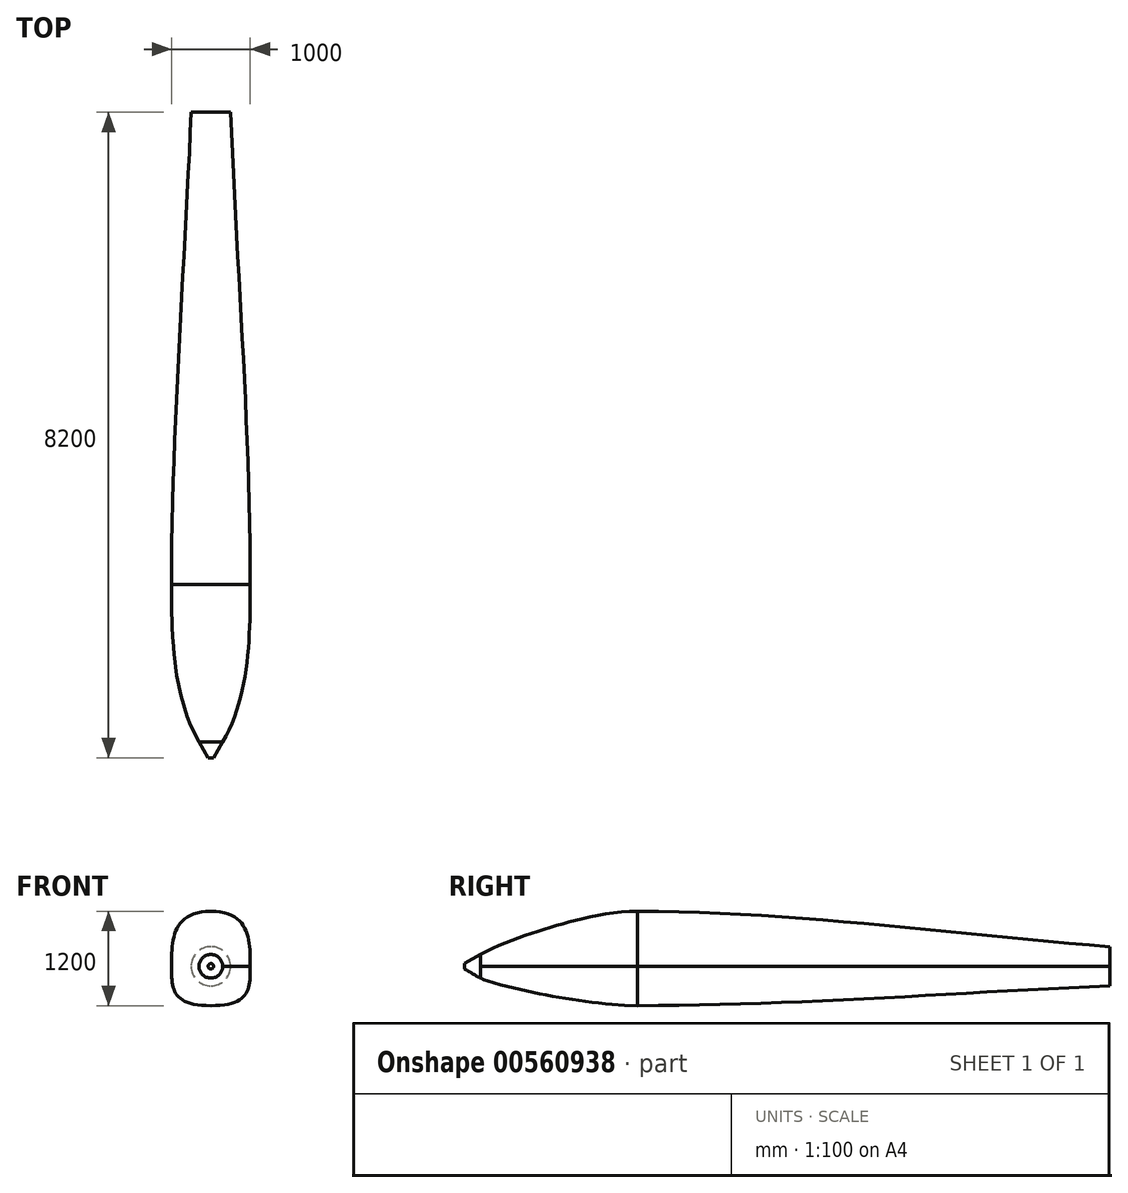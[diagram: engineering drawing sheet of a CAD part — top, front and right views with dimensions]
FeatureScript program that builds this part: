
annotation { "Feature Type Name" : "Feature", "Feature Type Description" : "" }
export const myFeature = defineFeature(function(context is Context, id is Id, definition is map)
    precondition{}
    {
        {
            var Q0;
            Q0=qCreatedBy(makeId("Front.planeOp"),FACE);
            var sketch = newSketch(context, id + "F0", { "sketchPlane" : qUnion([Q0])});
            skLineSegment(sketch, "E0.bottom", {"start": v(500, 700) * mm, "end": v(0, 700) * mm, "construction": true});
            skLineSegment(sketch, "E0.top", {"start": v(500, -500) * mm, "end": v(0, -500) * mm, "construction": true});
            skLineSegment(sketch, "E0.left", {"start": v(500, 700) * mm, "end": v(500, -500) * mm, "construction": true});
            skPoint(sketch, "E0.middle", {"position": v(0, 0) * mm});
            skLineSegment(sketch, "E1", {"start": v(0, 700) * mm, "end": v(0, 0) * mm, "construction": true});
            skLineSegment(sketch, "E2", {"start": v(0, 0) * mm, "end": v(0, -500) * mm, "construction": true});
            skFitSpline(sketch, "E3", {"points": [v(0, 700) * mm, v(500, 0) * mm, v(0, -500) * mm], "startDerivative": vector(2859.96, 0) * mm, "endDerivative": vector(-3154.46, 0) * mm});
            skFitSpline(sketch, "E4.MirrorCS", {"points": [v(0, 700) * mm, v(-500, 0) * mm, v(0, -500) * mm], "startDerivative": vector(-2859.96, 0) * mm, "endDerivative": vector(3154.46, 0) * mm});
            skSolve(sketch);
        }
        {
            var Q0;
            Q0=qCreatedBy(makeId("Front.planeOp"),FACE);
            cPlane(context, id + "F1", {"entities" : qUnion([Q0]), "cplaneType" : CPlaneType.OFFSET, "offset" : 2000 * mm, "width" : 150 * mm, "height" : 150 * mm});
        }
        {
            var Q0;
            Q0=qCreatedBy(id+"F1.planeOp",FACE);
            cPlane(context, id + "F2", {"entities" : qUnion([Q0]), "cplaneType" : CPlaneType.OFFSET, "offset" : 8000 * mm, "oppositeDirection" : true, "width" : 150 * mm, "height" : 150 * mm});
        }
        {
            var Q0;
            Q0=qCreatedBy(makeId("Right.planeOp"),FACE);
            cPlane(context, id + "F3", {"entities" : qUnion([Q0]), "cplaneType" : CPlaneType.OFFSET, "offset" : 3000 * mm, "width" : 150 * mm, "height" : 150 * mm});
        }
        {
            var Q0;
            Q0=qCreatedBy(id+"F1.planeOp",FACE);
            var sketch = newSketch(context, id + "F4", { "sketchPlane" : qUnion([Q0])});
            skCircle(sketch, "E5", {"center": v(0, 0) * mm, "radius": 150 * mm});
            skSolve(sketch);
        }
        {
            var Q0;
            Q0=makeQuery(id+"F4.imprint","IMPRINT",FACE,{"disambiguationData":[TD([[makeQuery(id+"F4.imprint","IMPRINT",EDGE,{"derivedFrom":sQuery(id+"F4.wireOp",EDGE,"E5")}),1.0]])]});
            extrude(context, id + "F5", {"entities" : qUnion([Q0]), "depth" : 200 * mm, "offsetDistance" : 25 * mm, "hasDraft" : true, "draftAngle" : 30 * degree, "draftPullDirection" : true});
        }
        {
            var Q0;
            Q0=qCreatedBy(id+"F2.planeOp",FACE);
            var sketch = newSketch(context, id + "F6", { "sketchPlane" : qUnion([Q0])});
            skCircle(sketch, "E6", {"center": v(0, 0) * mm, "radius": 250 * mm});
            skSolve(sketch);
        }
        {
            var Q0;
            Q0=qCreatedBy(makeId("Right.planeOp"),FACE);
            var sketch = newSketch(context, id + "F7", { "sketchPlane" : qUnion([Q0])});
            skPoint(sketch, "E7.0", {"position": v(0, -500) * mm});
            skLineSegment(sketch, "E8.0", {"start": v(-2000, -150) * mm, "end": v(-2000, 150) * mm, "construction": true});
            skPoint(sketch, "E9.0", {"position": v(0, 700) * mm});
            skFitSpline(sketch, "E10", {"points": [v(0, 700) * mm, v(-2000, 150) * mm], "startDerivative": vector(-2075.71, 0) * mm, "endDerivative": vector(-744.64, -429.92) * mm});
            skLineSegment(sketch, "E11", {"start": v(0, 700) * mm, "end": v(334.01, 700) * mm, "construction": true});
            skLineSegment(sketch, "E12", {"start": v(0, -500) * mm, "end": v(442.34, -500) * mm, "construction": true});
            skPoint(sketch, "E13.middle", {"position": v(-2000, 0) * mm});
            skFitSpline(sketch, "E14", {"points": [v(-2000, -150) * mm, v(0, -500) * mm], "startDerivative": vector(456.5, -263.56) * mm, "endDerivative": vector(2022.37, 0) * mm});
            skLineSegment(sketch, "E15", {"start": v(-2228.35, 18.16) * mm, "end": v(-1978.35, 162.5) * mm, "construction": true});
            skLineSegment(sketch, "E16", {"start": v(-1978.35, -162.5) * mm, "end": v(-2228.35, -18.16) * mm, "construction": true});
            skLineSegment(sketch, "E17", {"start": v(6000, -1790.84) * mm, "end": v(6000, 2998.88) * mm, "construction": true});
            skLineSegment(sketch, "E18", {"start": v(-4794.52, 0) * mm, "end": v(8752.85, 0) * mm, "construction": true});
            skPoint(sketch, "E19", {"position": v(6000, 0) * mm});
            skLineSegment(sketch, "E20.0", {"start": v(6000, -250) * mm, "end": v(6000, 250) * mm, "construction": true});
            skFitSpline(sketch, "E21", {"points": [v(0, 700) * mm, v(6000, 250) * mm], "startDerivative": vector(6013.8, 0) * mm, "endDerivative": vector(6000, -450) * mm});
            skFitSpline(sketch, "E22", {"points": [v(0, -500) * mm, v(6000, -250) * mm], "startDerivative": vector(6004.26, 0) * mm, "endDerivative": vector(6000, 250) * mm});
            skSolve(sketch);
        }
        {
            var Q0;
            Q0=qCreatedBy(makeId("Top.planeOp"),FACE);
            var sketch = newSketch(context, id + "F8", { "sketchPlane" : qUnion([Q0])});
            skLineSegment(sketch, "E23", {"start": v(-500, 0) * mm, "end": v(500, 0) * mm, "construction": true});
            skLineSegment(sketch, "E24", {"start": v(-34.53, -2200) * mm, "end": v(-150, -2000) * mm, "construction": true});
            skLineSegment(sketch, "E25", {"start": v(150, -2000) * mm, "end": v(34.53, -2200) * mm, "construction": true});
            skLineSegment(sketch, "E26", {"start": v(-500, 0) * mm, "end": v(-500, 662.87) * mm, "construction": true});
            skLineSegment(sketch, "E27", {"start": v(500, 0) * mm, "end": v(500, 620.99) * mm, "construction": true});
            skFitSpline(sketch, "E28", {"points": [v(500, 0) * mm, v(150, -2000) * mm], "startDerivative": vector(0, -2022.37) * mm, "endDerivative": vector(-1011.19, -1751.43) * mm});
            skLineSegment(sketch, "E29", {"start": v(0, 564.56) * mm, "end": v(0, -2822.28) * mm, "construction": true});
            skFitSpline(sketch, "E30.MirrorCS", {"points": [v(-500, 0) * mm, v(-150, -2000) * mm], "startDerivative": vector(0, -2022.37) * mm, "endDerivative": vector(1011.19, -1751.43) * mm});
            skLineSegment(sketch, "E31.0", {"start": v(250, 6000) * mm, "end": v(-250, 6000) * mm, "construction": true});
            skFitSpline(sketch, "E32", {"points": [v(500, 0) * mm, v(250, 6000) * mm], "startDerivative": vector(0, 6004.26) * mm, "endDerivative": vector(-250, 6000) * mm});
            skFitSpline(sketch, "E33.MirrorCS", {"points": [v(-500, 0) * mm, v(-250, 6000) * mm], "startDerivative": vector(0, 6004.26) * mm, "endDerivative": vector(250, 6000) * mm});
            skSolve(sketch);
        }
        {
            var Q0;
            Q0=makeQuery(id+"F0.imprint","IMPRINT",FACE,{"disambiguationData":[TD([[makeQuery(id+"F0.imprint","IMPRINT",EDGE,{"derivedFrom":sQuery(id+"F0.wireOp",EDGE,"E3")}),-1.0]])]});
            var Q1;
            Q1=makeQuery(id+"F5.opExtrude","CAP_FACE",FACE,{"disambiguationData":[OSD([sQuery(id+"F4.wireOp",EDGE,"E5")])],"isStart":true});
            var Q2;
            Q2=sQuery(id+"F7.wireOp",EDGE,"E10");
            var Q3;
            Q3=sQuery(id+"F8.wireOp",EDGE,"E28");
            var Q4;
            Q4=sQuery(id+"F8.wireOp",EDGE,"E30.MirrorCS");
            var Q5;
            Q5=sQuery(id+"F7.wireOp",EDGE,"E14");
            loft(context, id + "F9", {"addGuides" : true, "sheetProfilesArray" : [{ "sheetProfileEntities" : qUnion([Q0]) }, { "sheetProfileEntities" : qUnion([Q1]) }], "guidesArray" : [{ "guideEntities" : qUnion([Q2]), "guideDerivativeType" : LoftGuideDerivativeType.DEFAULT, "guideDerivativeMagnitude" : 1 }, { "guideEntities" : qUnion([Q3]), "guideDerivativeType" : LoftGuideDerivativeType.DEFAULT, "guideDerivativeMagnitude" : 1 }, { "guideEntities" : qUnion([Q4]), "guideDerivativeType" : LoftGuideDerivativeType.DEFAULT, "guideDerivativeMagnitude" : 1 }, { "guideEntities" : qUnion([Q5]), "guideDerivativeType" : LoftGuideDerivativeType.DEFAULT, "guideDerivativeMagnitude" : 1 }]});
        }
        {
            var Q1;
            Q1 = qSketchRegion(id + "F0", true);
            var Q2;
            Q2 = qSketchRegion(id + "F6", true);
            var Q3;
            Q3=sQuery(id+"F7.wireOp",EDGE,"E21");
            var Q4;
            Q4=sQuery(id+"F8.wireOp",EDGE,"E33.MirrorCS");
            var Q5;
            Q5=sQuery(id+"F7.wireOp",EDGE,"E22");
            var Q6;
            Q6=sQuery(id+"F8.wireOp",EDGE,"E32");
            loft(context, id + "F10", {"operationType" : NewBodyOperationType.ADD, "addGuides" : true, "sheetProfilesArray" : [{ "sheetProfileEntities" : qUnion([Q1]) }, { "sheetProfileEntities" : qUnion([Q2]) }], "guidesArray" : [{ "guideEntities" : qUnion([Q3]), "guideDerivativeType" : LoftGuideDerivativeType.DEFAULT, "guideDerivativeMagnitude" : 1 }, { "guideEntities" : qUnion([Q4]), "guideDerivativeType" : LoftGuideDerivativeType.DEFAULT, "guideDerivativeMagnitude" : 1 }, { "guideEntities" : qUnion([Q5]), "guideDerivativeType" : LoftGuideDerivativeType.DEFAULT, "guideDerivativeMagnitude" : 1 }, { "guideEntities" : qUnion([Q6]), "guideDerivativeType" : LoftGuideDerivativeType.DEFAULT, "guideDerivativeMagnitude" : 1 }]});
        }
        {
            var Q0;
            Q0=qCreatedBy(makeId("Right.planeOp"),FACE);
            var sketch = newSketch(context, id + "F11", { "sketchPlane" : qUnion([Q0])});
            skFitSpline(sketch, "E34", {"points": [v(-141.42, 0) * mm, v(5358.58, 0) * mm], "startDerivative": vector(0, 900) * mm, "endDerivative": vector(2335.4, 2.7) * mm});
            skFitSpline(sketch, "E35", {"points": [v(-141.42, 0) * mm, v(5358.58, 0) * mm], "startDerivative": vector(0, -600) * mm, "endDerivative": vector(2335.81, 0) * mm});
            skSolve(sketch);
        }
        {
            var Q0;
            Q0=qCreatedBy(id+"F3.planeOp",FACE);
            var sketch = newSketch(context, id + "F12", { "sketchPlane" : qUnion([Q0])});
            skFitSpline(sketch, "E36", {"points": [v(3658.58, 0) * mm, v(5158.58, 0) * mm], "startDerivative": vector(0, 300) * mm, "endDerivative": vector(1614.07, -104.6) * mm});
            skFitSpline(sketch, "E37", {"points": [v(3658.58, 0) * mm, v(5158.58, 0) * mm], "startDerivative": vector(0, -200) * mm, "endDerivative": vector(1486.5, 111.78) * mm});
            skLineSegment(sketch, "E38", {"start": v(3658.58, 0) * mm, "end": v(5158.58, 0) * mm, "construction": true});
            skSolve(sketch);
        }
        {
            var Q0;
            Q0=qCreatedBy(makeId("Top.planeOp"),FACE);
            var sketch = newSketch(context, id + "F13", { "sketchPlane" : qUnion([Q0])});
            skPoint(sketch, "E39.0", {"position": v(0, -141.42) * mm});
            skPoint(sketch, "E40.0", {"position": v(0, 5358.58) * mm});
            skPoint(sketch, "E41.0", {"position": v(3000, 3658.58) * mm});
            skPoint(sketch, "E42.0", {"position": v(3000, 5158.58) * mm});
            skLineSegment(sketch, "E43", {"start": v(3000, 5158.58) * mm, "end": v(0, 5358.58) * mm});
            skLineSegment(sketch, "E44", {"start": v(3000, 3658.58) * mm, "end": v(0, -141.42) * mm});
            skSolve(sketch);
        }
        {
            var Q0;
            Q0=sQuery(id+"F13.wireOp",EDGE,"E44");
            var Q1;
            Q1=sQuery(id+"F13.wireOp",EDGE,"E43");
            var Q2;
            Q2=sQuery(id+"F12.wireOp",EDGE,"E36");
            var Q3;
            Q3=sQuery(id+"F11.wireOp",EDGE,"E34");
            loft(context, id + "F14", {"bodyType" : ToolBodyType.SURFACE, "addGuides" : true, "wireProfilesArray" : [{ "wireProfileEntities" : qUnion([Q0]) }, { "wireProfileEntities" : qUnion([Q1]) }], "guidesArray" : [{ "guideEntities" : qUnion([Q2]), "guideDerivativeType" : LoftGuideDerivativeType.DEFAULT, "guideDerivativeMagnitude" : 1 }, { "guideEntities" : qUnion([Q3]), "guideDerivativeType" : LoftGuideDerivativeType.DEFAULT, "guideDerivativeMagnitude" : 1 }]});
        }
        {
            var Q0;
            Q0=sQuery(id+"F13.wireOp",EDGE,"E44");
            var Q1;
            Q1=sQuery(id+"F13.wireOp",EDGE,"E43");
            var Q2;
            Q2=sQuery(id+"F11.wireOp",EDGE,"E35");
            var Q3;
            Q3=sQuery(id+"F12.wireOp",EDGE,"E37");
            loft(context, id + "F15", {"bodyType" : ToolBodyType.SURFACE, "addGuides" : true, "wireProfilesArray" : [{ "wireProfileEntities" : qUnion([Q0]) }, { "wireProfileEntities" : qUnion([Q1]) }], "guidesArray" : [{ "guideEntities" : qUnion([Q2]), "guideDerivativeType" : LoftGuideDerivativeType.DEFAULT, "guideDerivativeMagnitude" : 1 }, { "guideEntities" : qUnion([Q3]), "guideDerivativeType" : LoftGuideDerivativeType.DEFAULT, "guideDerivativeMagnitude" : 1 }]});
        }
    });
